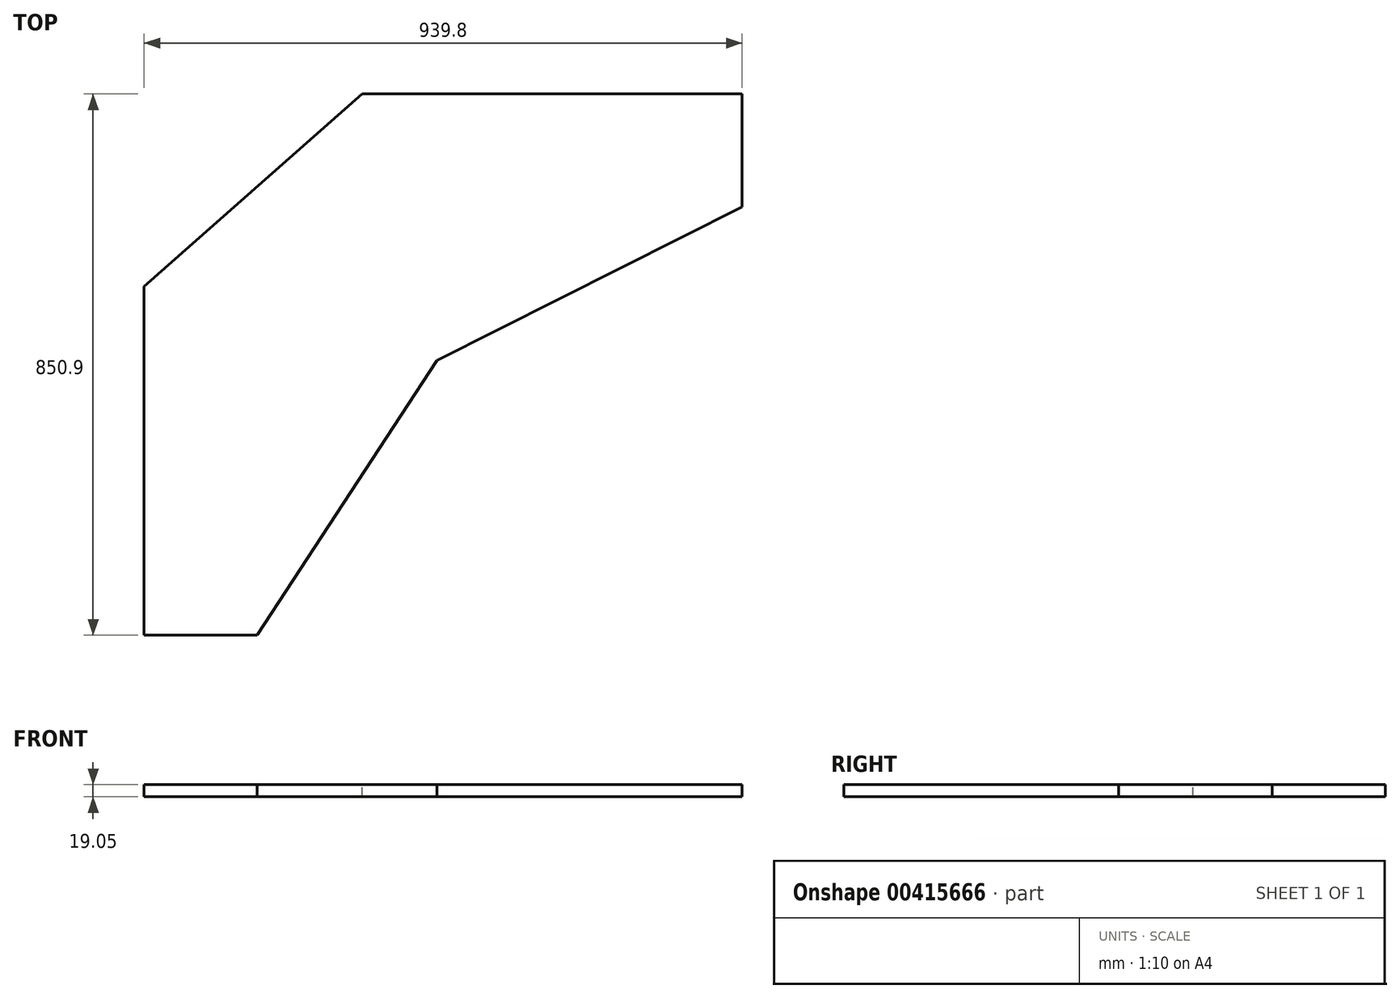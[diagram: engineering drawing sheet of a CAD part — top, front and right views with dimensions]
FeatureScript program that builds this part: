
annotation { "Feature Type Name" : "Feature", "Feature Type Description" : "" }
export const myFeature = defineFeature(function(context is Context, id is Id, definition is map)
    precondition{}
    {
        {
            var Q0;
            Q0=qCreatedBy(makeId("Top.planeOp"),FACE);
            var sketch = newSketch(context, id + "F0", { "sketchPlane" : qUnion([Q0])});
            skLineSegment(sketch, "E0", {"start": v(-235.73, -97.64) * mm, "end": v(-962.03, 628.65) * mm, "construction": true});
            skLineSegment(sketch, "E1", {"start": v(-962.02, -222.25) * mm, "end": v(-784.22, -222.25) * mm});
            skLineSegment(sketch, "E2", {"start": v(-22.22, 450.85) * mm, "end": v(-22.22, 628.65) * mm});
            skLineSegment(sketch, "E3", {"start": v(-22.22, 628.65) * mm, "end": v(-619.37, 628.65) * mm});
            skLineSegment(sketch, "E4", {"start": v(-619.37, 628.65) * mm, "end": v(-962.02, 325.97) * mm});
            skLineSegment(sketch, "E5", {"start": v(-962.02, 325.97) * mm, "end": v(-962.02, -222.25) * mm});
            skLineSegment(sketch, "E6", {"start": v(-784.22, -222.25) * mm, "end": v(-501.65, 209.55) * mm});
            skPoint(sketch, "E6.endSnap0", {"position": v(-584.04, 209.55) * mm});
            skLineSegment(sketch, "E7", {"start": v(-501.65, 209.55) * mm, "end": v(-22.22, 450.85) * mm});
            skLineSegment(sketch, "E8", {"start": v(-784.22, -222.25) * mm, "end": v(-22.22, 450.85) * mm, "construction": true});
            skSolve(sketch);
        }
        {
            var Q0;
            Q0 = qSketchRegion(id + "F0", true);
            extrude(context, id + "F1", {"entities" : qUnion([Q0]), "oppositeDirection" : true, "depth" : 19.05 * mm});
        }
    });
